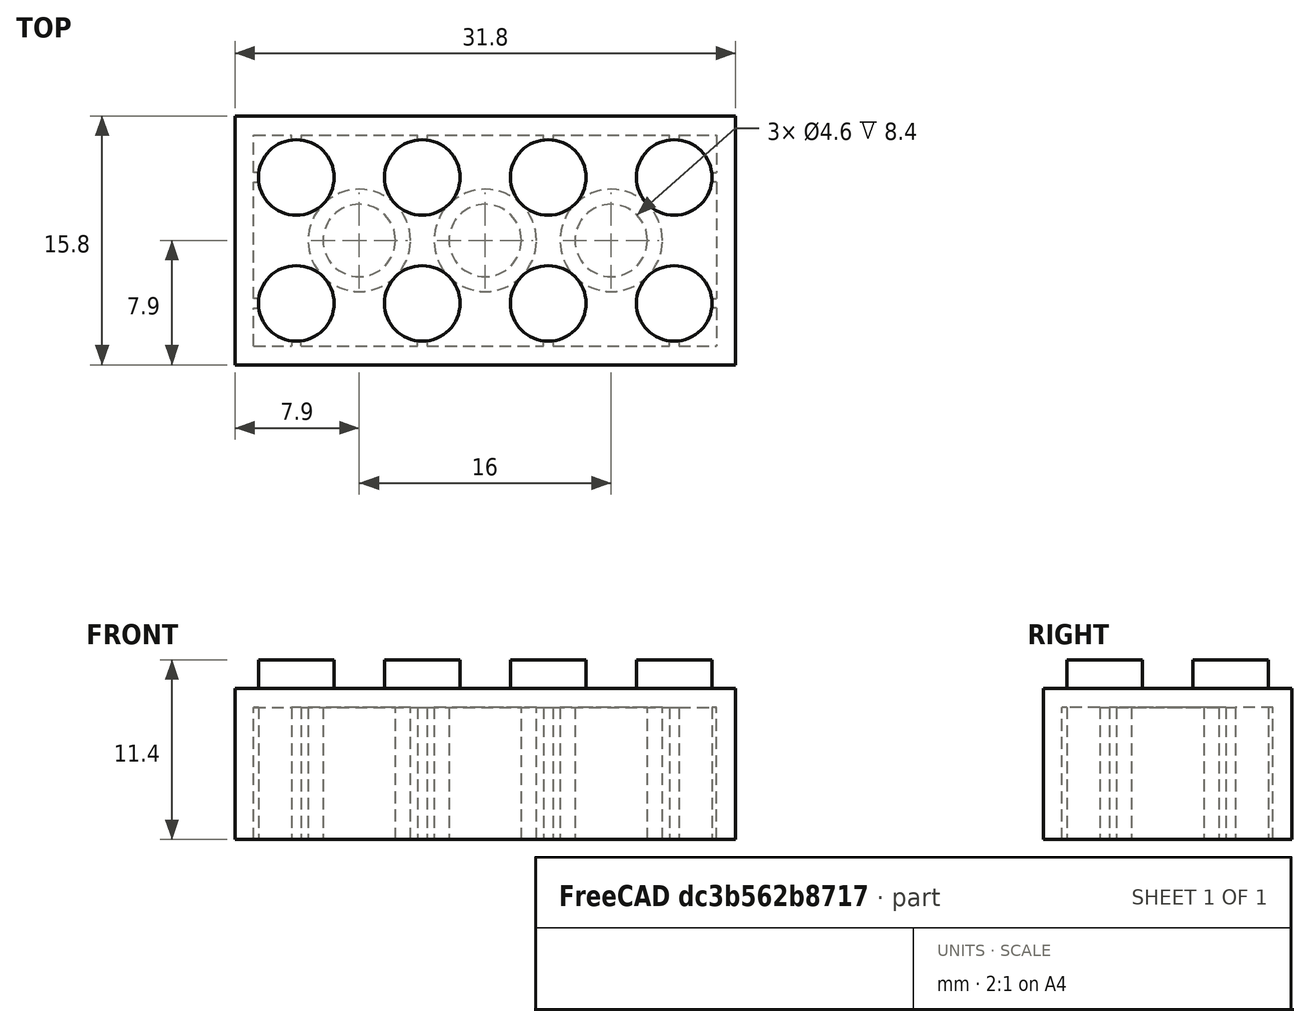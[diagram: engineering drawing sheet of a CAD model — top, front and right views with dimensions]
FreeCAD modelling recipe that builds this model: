
FCSTD DOCUMENT  (FreeCAD 0.20R29410 (Git))
Label: lego_brick
License: All rights reserved
LicenseURL: http://en.wikipedia.org/wiki/All_rights_reserved
objects: TechDraw::DrawViewDimension×13, Sketcher::SketchObject×4, TechDraw::DrawProjGroupItem×4, PartDesign::Pad×3, PartDesign::Pocket×1, PartDesign::Body×1, TechDraw::DrawSVGTemplate×1, TechDraw::DrawViewPart×1, TechDraw::DrawProjGroup×1, TechDraw::DrawViewAnnotation×1, TechDraw::DrawPage×1
note: 13 computed .brp shape members not serialized (recipe doc carries the construction recipe); baked Part::Feature solids carry a one-line shape summary decoded from their .brp

FEATURE [Sketcher::SketchObject] Sketch
  FullyConstrained = true
  MapMode = 5
  Support = -> [XY_Plane]
  sketch-geometry (5):
    g0: LineSegment StartX=-15.9 StartY=7.9 StartZ=0 EndX=-15.9 EndY=-7.9 EndZ=0
    g1: LineSegment StartX=-15.9 StartY=-7.9 StartZ=0 EndX=15.9 EndY=-7.9 EndZ=0
    g2: LineSegment StartX=15.9 StartY=-7.9 StartZ=0 EndX=15.9 EndY=7.9 EndZ=0
    g3: LineSegment StartX=15.9 StartY=7.9 StartZ=0 EndX=-15.9 EndY=7.9 EndZ=0
    g4: GeomPoint X=0 Y=0 Z=0
  constraints (12):
    c: Coincident(g0,g1)
    c: Coincident(g1,g2)
    c: Coincident(g2,g3)
    c: Coincident(g3,g0)
    c: Horizontal(g1)
    c: Horizontal(g3)
    c: Vertical(g0)
    c: Vertical(g2)
    c: Symmetric(g1,g0,g4)
    c: Coincident(g4,g-1)
    c: DistanceY(g2,g2) = 15.8
    c: DistanceX(g3,g3) = 31.8
FEATURE [PartDesign::Pad] Pad
  Direction = (0,0,1)
  Length = 9.6
  Length2 = 10
  Profile = -> Sketch
  ReferenceAxis = -> Sketch [N_Axis]
  Type = 0
FEATURE [Sketcher::SketchObject] Sketch001
  ExternalGeometry = -> [Pad]
  FullyConstrained = true
  MapMode = 5
  Placement = pos=(0,0,9.6) rot=(0,0,1;0rad)
  Support = -> [Pad]
  sketch-geometry (8):
    g0: Circle CenterX=-12 CenterY=4 CenterZ=0 NormalX=0 NormalY=0 NormalZ=1 AngleXU=0 Radius=2.4
    g1: Circle CenterX=-4 CenterY=4 CenterZ=0 NormalX=0 NormalY=0 NormalZ=1 AngleXU=0 Radius=2.4
    g2: Circle CenterX=4 CenterY=4 CenterZ=0 NormalX=0 NormalY=0 NormalZ=1 AngleXU=0 Radius=2.4
    g3: Circle CenterX=12 CenterY=4 CenterZ=0 NormalX=0 NormalY=0 NormalZ=1 AngleXU=0 Radius=2.4
    g4: Circle CenterX=12 CenterY=-4 CenterZ=0 NormalX=0 NormalY=0 NormalZ=1 AngleXU=0 Radius=2.4
    g5: Circle CenterX=4 CenterY=-4 CenterZ=0 NormalX=0 NormalY=0 NormalZ=1 AngleXU=0 Radius=2.4
    g6: Circle CenterX=-4 CenterY=-4 CenterZ=0 NormalX=0 NormalY=0 NormalZ=1 AngleXU=0 Radius=2.4
    g7: Circle CenterX=-12 CenterY=-4 CenterZ=0 NormalX=0 NormalY=0 NormalZ=1 AngleXU=0 Radius=2.4
  constraints (20):
    c: Diameter(g0) = 4.8
    c: Equal(g0,g1)
    c: Equal(g1,g2)
    c: Equal(g2,g3)
    c: Equal(g3,g4)
    c: Equal(g4,g5)
    c: Equal(g5,g6)
    c: Equal(g6,g7)
    c: Symmetric(g0,g7,g-1)
    c: Symmetric(g1,g6,g-1)
    c: Symmetric(g2,g5,g-1)
    c: Symmetric(g3,g4,g-1)
    c: DistanceX(g-3,g0) = 3.9
    c: DistanceY(g0,g-3) = 3.9
    c: DistanceX(g0,g1) = 8
    c: DistanceX(g1,g2) = 8
    c: DistanceX(g2,g3) = 8
    c: Horizontal(g1,g0)
    c: Horizontal(g2,g1)
    c: Horizontal(g3,g2)
FEATURE [PartDesign::Pad] Pad001
  BaseFeature = -> Pad
  Direction = (0,0,1)
  Length = 1.8
  Length2 = 10
  Profile = -> Sketch001
  ReferenceAxis = -> Sketch001 [N_Axis]
  Type = 0
FEATURE [Sketcher::SketchObject] Sketch002
  ExternalGeometry = -> [Pad001]
  FullyConstrained = true
  MapMode = 5
  Placement = pos=(0,0,0) rot=(1,0,0;3.14159rad)
  Support = -> [Pad001]
  sketch-geometry (11):
    g0: LineSegment StartX=-14.7 StartY=6.7 StartZ=0 EndX=-14.7 EndY=-6.7 EndZ=0
    g1: LineSegment StartX=-14.7 StartY=-6.7 StartZ=0 EndX=14.7 EndY=-6.7 EndZ=0
    g2: LineSegment StartX=14.7 StartY=-6.7 StartZ=0 EndX=14.7 EndY=6.7 EndZ=0
    g3: GeomPoint X=0 Y=0 Z=0
    g4: Circle CenterX=0 CenterY=0 CenterZ=0 NormalX=0 NormalY=0 NormalZ=1 AngleXU=0 Radius=2.3
    g5: Circle CenterX=0 CenterY=0 CenterZ=0 NormalX=0 NormalY=0 NormalZ=1 AngleXU=0 Radius=3.25
    g6: Circle CenterX=8 CenterY=0 CenterZ=0 NormalX=0 NormalY=0 NormalZ=1 AngleXU=0 Radius=2.3
    g7: Circle CenterX=8 CenterY=0 CenterZ=0 NormalX=0 NormalY=0 NormalZ=1 AngleXU=0 Radius=3.25
    g8: Circle CenterX=-8 CenterY=0 CenterZ=0 NormalX=0 NormalY=0 NormalZ=1 AngleXU=0 Radius=2.3
    g9: Circle CenterX=-8 CenterY=0 CenterZ=0 NormalX=0 NormalY=0 NormalZ=1 AngleXU=0 Radius=3.25
    g10: LineSegment StartX=-14.7 StartY=6.7 StartZ=0 EndX=14.7 EndY=6.7 EndZ=0
  constraints (26):
    c: Coincident(g0,g1)
    c: Coincident(g1,g2)
    c: Horizontal(g1)
    c: Vertical(g0)
    c: Vertical(g2)
    c: Symmetric(g1,g0,g3)
    c: Coincident(g3,g-1)
    c: DistanceX(g-3,g0) = 1.2
    c: DistanceY(g0,g-3) = 1.2
    c: Coincident(g4,g3)
    c: Diameter(g4) = 4.6
    c: Coincident(g5,g4)
    c: Diameter(g5) = 6.5
    c: PointOnObject(g6,g-1)
    c: Coincident(g7,g6)
    c: PointOnObject(g8,g-1)
    c: Coincident(g9,g8)
    c: Equal(g8,g6)
    c: Equal(g6,g4)
    c: Equal(g9,g5)
    c: Equal(g5,g7)
    c: DistanceX(g4,g6) = 8
    c: DistanceX(g8,g4) = 8
    c: Coincident(g10,g0)
    c: Coincident(g10,g2)
    c: Horizontal(g10)
FEATURE [PartDesign::Pocket] Pocket
  BaseFeature = -> Pad001
  Direction = (0,0,1)
  Length = 8.4
  Length2 = 5
  Profile = -> Sketch002
  ReferenceAxis = -> Sketch002 [N_Axis]
  Type = 0
FEATURE [Sketcher::SketchObject] Sketch003
  ExternalGeometry = -> [Pocket]
  FullyConstrained = true
  MapMode = 5
  Placement = pos=(0,0,8.4) rot=(1,0,0;3.14159rad)
  Support = -> [Pocket]
  sketch-geometry (48):
    g0: LineSegment StartX=-12.3 StartY=6.7 StartZ=0 EndX=-11.7 EndY=6.7 EndZ=0
    g1: LineSegment StartX=-11.7 StartY=6.7 StartZ=0 EndX=-11.7 EndY=6.4 EndZ=0
    g2: LineSegment StartX=-11.7 StartY=6.4 StartZ=0 EndX=-12.3 EndY=6.4 EndZ=0
    g3: LineSegment StartX=-12.3 StartY=6.4 StartZ=0 EndX=-12.3 EndY=6.7 EndZ=0
    g4: LineSegment StartX=4.3 StartY=6.7 StartZ=0 EndX=3.7 EndY=6.7 EndZ=0
    g5: LineSegment StartX=3.7 StartY=6.7 StartZ=0 EndX=3.7 EndY=6.4 EndZ=0
    g6: LineSegment StartX=3.7 StartY=6.4 StartZ=0 EndX=4.3 EndY=6.4 EndZ=0
    g7: LineSegment StartX=4.3 StartY=6.4 StartZ=0 EndX=4.3 EndY=6.7 EndZ=0
    g8: LineSegment StartX=-3.7 StartY=6.7 StartZ=0 EndX=-4.3 EndY=6.7 EndZ=0
    g9: LineSegment StartX=-4.3 StartY=6.7 StartZ=0 EndX=-4.3 EndY=6.4 EndZ=0
    g10: LineSegment StartX=-4.3 StartY=6.4 StartZ=0 EndX=-3.7 EndY=6.4 EndZ=0
    g11: LineSegment StartX=-3.7 StartY=6.4 StartZ=0 EndX=-3.7 EndY=6.7 EndZ=0
    g12: LineSegment StartX=12.3 StartY=6.7 StartZ=0 EndX=11.7 EndY=6.7 EndZ=0
    g13: LineSegment StartX=11.7 StartY=6.7 StartZ=0 EndX=11.7 EndY=6.4 EndZ=0
    g14: LineSegment StartX=11.7 StartY=6.4 StartZ=0 EndX=12.3 EndY=6.4 EndZ=0
    g15: LineSegment StartX=12.3 StartY=6.4 StartZ=0 EndX=12.3 EndY=6.7 EndZ=0
    g16: LineSegment StartX=-14.7 StartY=4.3 StartZ=0 EndX=-14.4 EndY=4.3 EndZ=0
    g17: LineSegment StartX=-14.4 StartY=4.3 StartZ=0 EndX=-14.4 EndY=3.7 EndZ=0
    g18: LineSegment StartX=-14.4 StartY=3.7 StartZ=0 EndX=-14.7 EndY=3.7 EndZ=0
    g19: LineSegment StartX=-14.7 StartY=3.7 StartZ=0 EndX=-14.7 EndY=4.3 EndZ=0
    g20: LineSegment StartX=-14.7 StartY=-3.7 StartZ=0 EndX=-14.4 EndY=-3.7 EndZ=0
    g21: LineSegment StartX=-14.4 StartY=-3.7 StartZ=0 EndX=-14.4 EndY=-4.3 EndZ=0
    g22: LineSegment StartX=-14.4 StartY=-4.3 StartZ=0 EndX=-14.7 EndY=-4.3 EndZ=0
    g23: LineSegment StartX=-14.7 StartY=-4.3 StartZ=0 EndX=-14.7 EndY=-3.7 EndZ=0
    g24: LineSegment StartX=-12.3 StartY=-6.7 StartZ=0 EndX=-11.7 EndY=-6.7 EndZ=0
    g25: LineSegment StartX=-11.7 StartY=-6.7 StartZ=0 EndX=-11.7 EndY=-6.4 EndZ=0
    g26: LineSegment StartX=-11.7 StartY=-6.4 StartZ=0 EndX=-12.3 EndY=-6.4 EndZ=0
    g27: LineSegment StartX=-12.3 StartY=-6.4 StartZ=0 EndX=-12.3 EndY=-6.7 EndZ=0
    g28: LineSegment StartX=-4.3 StartY=-6.7 StartZ=0 EndX=-3.7 EndY=-6.7 EndZ=0
    g29: LineSegment StartX=-3.7 StartY=-6.7 StartZ=0 EndX=-3.7 EndY=-6.4 EndZ=0
    g30: LineSegment StartX=-3.7 StartY=-6.4 StartZ=0 EndX=-4.3 EndY=-6.4 EndZ=0
    g31: LineSegment StartX=-4.3 StartY=-6.4 StartZ=0 EndX=-4.3 EndY=-6.7 EndZ=0
    g32: LineSegment StartX=3.7 StartY=-6.7 StartZ=0 EndX=4.3 EndY=-6.7 EndZ=0
    g33: LineSegment StartX=4.3 StartY=-6.7 StartZ=0 EndX=4.3 EndY=-6.4 EndZ=0
    g34: LineSegment StartX=4.3 StartY=-6.4 StartZ=0 EndX=3.7 EndY=-6.4 EndZ=0
    g35: LineSegment StartX=3.7 StartY=-6.4 StartZ=0 EndX=3.7 EndY=-6.7 EndZ=0
    g36: LineSegment StartX=11.7 StartY=-6.7 StartZ=0 EndX=12.3 EndY=-6.7 EndZ=0
    g37: LineSegment StartX=12.3 StartY=-6.7 StartZ=0 EndX=12.3 EndY=-6.4 EndZ=0
    g38: LineSegment StartX=12.3 StartY=-6.4 StartZ=0 EndX=11.7 EndY=-6.4 EndZ=0
    g39: LineSegment StartX=11.7 StartY=-6.4 StartZ=0 EndX=11.7 EndY=-6.7 EndZ=0
    g40: LineSegment StartX=14.7 StartY=4.3 StartZ=0 EndX=14.4 EndY=4.3 EndZ=0
    g41: LineSegment StartX=14.4 StartY=4.3 StartZ=0 EndX=14.4 EndY=3.7 EndZ=0
    g42: LineSegment StartX=14.4 StartY=3.7 StartZ=0 EndX=14.7 EndY=3.7 EndZ=0
    g43: LineSegment StartX=14.7 StartY=3.7 StartZ=0 EndX=14.7 EndY=4.3 EndZ=0
    g44: LineSegment StartX=14.7 StartY=-3.7 StartZ=0 EndX=14.4 EndY=-3.7 EndZ=0
    g45: LineSegment StartX=14.4 StartY=-3.7 StartZ=0 EndX=14.4 EndY=-4.3 EndZ=0
    g46: LineSegment StartX=14.4 StartY=-4.3 StartZ=0 EndX=14.7 EndY=-4.3 EndZ=0
    g47: LineSegment StartX=14.7 StartY=-4.3 StartZ=0 EndX=14.7 EndY=-3.7 EndZ=0
  constraints (137):
    c: Coincident(g0,g1)
    c: Coincident(g1,g2)
    c: Coincident(g2,g3)
    c: Coincident(g3,g0)
    c: Horizontal(g0)
    c: Horizontal(g2)
    c: Vertical(g1)
    c: Vertical(g3)
    c: DistanceX(g-3,g0) = 3.6
    c: Coincident(g4,g5)
    c: Coincident(g5,g6)
    c: Coincident(g6,g7)
    c: Coincident(g7,g4)
    c: Horizontal(g4)
    c: Horizontal(g6)
    c: Vertical(g5)
    c: Vertical(g7)
    c: PointOnObject(g4,g-8)
    c: Coincident(g8,g9)
    c: Coincident(g9,g10)
    c: Coincident(g10,g11)
    c: Coincident(g11,g8)
    c: Horizontal(g8)
    c: Horizontal(g10)
    c: Vertical(g9)
    c: Vertical(g11)
    c: Coincident(g12,g13)
    c: Coincident(g13,g14)
    c: Coincident(g14,g15)
    c: Coincident(g15,g12)
    c: Horizontal(g12)
    c: Horizontal(g14)
    c: Vertical(g13)
    c: Vertical(g15)
    c: PointOnObject(g12,g-8)
    c: DistanceY(g2,g0) = 0.3
    c: DistanceX(g0,g0) = 0.6
    c: Equal(g2,g6)
    c: Equal(g6,g10)
    c: Equal(g10,g14)
    c: Equal(g1,g5)
    c: Equal(g9,g13)
    c: Symmetric(g4,g8,g-2)
    c: DistanceX(g-3,g8) = 11.6
    c: Coincident(g16,g17)
    c: Coincident(g17,g18)
    c: Coincident(g18,g19)
    c: Coincident(g19,g16)
    c: Horizontal(g16)
    c: Horizontal(g18)
    c: Vertical(g17)
    c: Vertical(g19)
    c: PointOnObject(g16,g-4)
    c: Coincident(g20,g21)
    c: Coincident(g21,g22)
    c: Coincident(g22,g23)
    c: Coincident(g23,g20)
    c: Horizontal(g20)
    c: Horizontal(g22)
    c: Vertical(g21)
    c: Vertical(g23)
    c: PointOnObject(g20,g-4)
    c: DistanceY(g18,g16) = 0.6
    c: DistanceX(g16,g16) = 0.3
    c: Equal(g18,g20)
    c: Equal(g21,g17)
    c: DistanceY(g16,g-3) = 3.6
    c: DistanceY(g-9,g22) = 3.6
    c: Coincident(g24,g25)
    c: Coincident(g25,g26)
    c: Coincident(g26,g27)
    c: Coincident(g27,g24)
    c: Horizontal(g24)
    c: Horizontal(g26)
    c: Vertical(g25)
    c: Vertical(g27)
    c: PointOnObject(g24,g-5)
    c: Coincident(g28,g29)
    c: Coincident(g29,g30)
    c: Coincident(g30,g31)
    c: Coincident(g31,g28)
    c: Horizontal(g28)
    c: Horizontal(g30)
    c: Vertical(g29)
    c: Vertical(g31)
    c: PointOnObject(g28,g-5)
    c: Coincident(g32,g33)
    c: Coincident(g33,g34)
    c: Coincident(g34,g35)
    c: Coincident(g35,g32)
    c: Horizontal(g32)
    c: Horizontal(g34)
    c: Vertical(g33)
    c: Vertical(g35)
    c: Coincident(g36,g37)
    c: Coincident(g37,g38)
    c: Coincident(g38,g39)
    c: Coincident(g39,g36)
    c: Horizontal(g36)
    c: Horizontal(g38)
    c: Vertical(g37)
    c: Vertical(g39)
    c: PointOnObject(g36,g-5)
    c: Equal(g38,g14)
    c: Equal(g14,g34)
    c: Equal(g34,g30)
    c: Equal(g30,g26)
    c: Equal(g37,g7)
    c: Equal(g7,g33)
    c: Symmetric(g2,g26,g-1)
    c: Symmetric(g30,g9,g-1)
    c: Symmetric(g34,g5,g-1)
    c: Symmetric(g38,g13,g-1)
    c: Coincident(g40,g41)
    c: Coincident(g41,g42)
    c: Coincident(g42,g43)
    c: Coincident(g43,g40)
    c: Horizontal(g40)
    c: Horizontal(g42)
    c: Vertical(g41)
    c: Vertical(g43)
    c: PointOnObject(g40,g-6)
    c: Coincident(g44,g45)
    c: Coincident(g45,g46)
    c: Coincident(g46,g47)
    c: Coincident(g47,g44)
    c: Horizontal(g44)
    c: Horizontal(g46)
    c: Vertical(g45)
    c: Vertical(g47)
    c: PointOnObject(g44,g-6)
    c: Equal(g17,g41)
    c: Equal(g41,g45)
    c: Symmetric(g40,g16,g-2)
    c: Symmetric(g45,g21,g-2)
    c: DistanceX(g12,g-7) = 3.6
    c: PointOnObject(g0,g-8)
FEATURE [PartDesign::Pad] Pad002
  BaseFeature = -> Pocket
  Direction = (0,0,-1)
  Length = 8.4
  Length2 = 10
  Profile = -> Sketch003
  ReferenceAxis = -> Sketch003 [N_Axis]
  Type = 0
FEATURE [PartDesign::Body] Body  label="LegoBrick2x4"
  Group = -> [Sketch,Pad,Sketch001,Pad001,Sketch002,Pocket,Sketch003,Pad002]
  Origin = -> Origin
  Tip = -> Pad002
FEATURE [TechDraw::DrawSVGTemplate] Template
  Height = 297
  Orientation = 0
  Width = 210
FEATURE [TechDraw::DrawViewPart] View
  Caption = 3D View
  CoarseView = false
  Direction = (0.378,-0.742,0.554)
  Focus = 100
  HardHidden = false
  IsoCount = 0
  IsoHidden = false
  IsoVisible = false
  LockPosition = false
  Perspective = false
  Rotation = 0
  Scale = 2
  ScaleType = 2
  SeamHidden = false
  SeamVisible = true
  SmoothHidden = false
  SmoothVisible = true
  Source = -> [Body]
  X = 58.5961
  XDirection = (0.887,0.462,0.013)
  Y = 233.477
FEATURE [TechDraw::DrawProjGroupItem] ProjItem  label="Front"
  Caption = Front View
  CoarseView = false
  Direction = (0,-1,0)
  Focus = 100
  HardHidden = false
  IsoCount = 0
  IsoHidden = false
  IsoVisible = false
  LockPosition = true
  Perspective = false
  Rotation = 0
  RotationVector = (1,0,0)
  ScaleType = 2
  SeamHidden = false
  SeamVisible = true
  SmoothHidden = false
  SmoothVisible = true
  Source = -> [Body]
  Type = 0
  X = 0
  XDirection = (1,0,2e-16)
  Y = 0
FEATURE [TechDraw::DrawProjGroupItem] ProjItem001  label="Right"
  Caption = Left View
  CoarseView = false
  Direction = (1,-1e-16,2e-16)
  Focus = 100
  HardHidden = false
  IsoCount = 0
  IsoHidden = false
  IsoVisible = false
  LockPosition = false
  Perspective = false
  Rotation = 0
  RotationVector = (1,0,0)
  ScaleType = 2
  SeamHidden = false
  SeamVisible = true
  SmoothHidden = false
  SmoothVisible = true
  Source = -> [Body]
  Type = 2
  X = -52.0285
  XDirection = (1e-16,1,0)
  Y = 0
FEATURE [TechDraw::DrawProjGroupItem] ProjItem003  label="Top"
  Caption = Top View
  CoarseView = false
  Direction = (-2e-16,0,1)
  Focus = 100
  HardHidden = false
  IsoCount = 0
  IsoHidden = false
  IsoVisible = false
  LockPosition = false
  Perspective = false
  Rotation = 0
  RotationVector = (1,0,0)
  ScaleType = 2
  SeamHidden = false
  SeamVisible = true
  SmoothHidden = false
  SmoothVisible = true
  Source = -> [Body]
  Type = 4
  X = 0
  XDirection = (1,0,2e-16)
  Y = 38.3342
FEATURE [TechDraw::DrawProjGroupItem] ProjItem004  label="Bottom"
  Caption = Bottom View
  CoarseView = false
  Direction = (2e-16,0,-1)
  Focus = 100
  HardHidden = false
  IsoCount = 0
  IsoHidden = false
  IsoVisible = false
  LockPosition = false
  Perspective = false
  Rotation = 0
  RotationVector = (1,0,0)
  ScaleType = 2
  SeamHidden = false
  SeamVisible = true
  SmoothHidden = false
  SmoothVisible = true
  Source = -> [Body]
  Type = 5
  X = 0
  XDirection = (1,0,2e-16)
  Y = -57.8041
FEATURE [TechDraw::DrawProjGroup] ProjGroup
  Anchor = -> ProjItem
  AutoDistribute = false
  LockPosition = false
  ProjectionType = 0
  Rotation = 0
  ScaleType = 2
  Source = -> [Body]
  Views = -> [ProjItem,ProjItem001,ProjItem003,ProjItem004]
  X = 110.766
  Y = 108.956
  spacingX = 10
  spacingY = 15
FEATURE [TechDraw::DrawViewDimension] Dimension003
  AngleOverride = false
  Arbitrary = false
  ArbitraryTolerances = false
  EqualTolerance = true
  ExtensionAngle = 0
  FormatSpec = %.2w
  FormatSpecOverTolerance = %+.2w
  FormatSpecUnderTolerance = %+.2w
  Inverted = false
  LineAngle = 0
  LockPosition = false
  MeasureType = 1
  OverTolerance = 0
  References2D = -> [ProjItem003]
  Rotation = 0
  ScaleType = 0
  TheoreticalExact = false
  Type = 1
  UnderTolerance = 0
  X = -24.2592
  Y = 27.8106
FEATURE [TechDraw::DrawViewDimension] Dimension004
  AngleOverride = false
  Arbitrary = false
  ArbitraryTolerances = false
  EqualTolerance = true
  ExtensionAngle = 0
  FormatSpec = %.2w
  FormatSpecOverTolerance = %+.2w
  FormatSpecUnderTolerance = %+.2w
  Inverted = false
  LineAngle = 0
  LockPosition = false
  MeasureType = 1
  OverTolerance = 0
  References2D = -> [ProjItem003]
  Rotation = 0
  ScaleType = 0
  TheoreticalExact = false
  Type = 1
  UnderTolerance = 0
  X = -0.11096
  Y = 37.5852
FEATURE [TechDraw::DrawViewDimension] Dimension
  AngleOverride = false
  Arbitrary = false
  ArbitraryTolerances = false
  EqualTolerance = true
  ExtensionAngle = 0
  FormatSpec = %.2w
  FormatSpecOverTolerance = %+.2w
  FormatSpecUnderTolerance = %+.2w
  Inverted = false
  LineAngle = 0
  LockPosition = false
  MeasureType = 1
  OverTolerance = 0
  References2D = -> [ProjItem003]
  Rotation = 0
  ScaleType = 0
  TheoreticalExact = false
  Type = 2
  UnderTolerance = 0
  X = -34.7789
  Y = -7.10758
FEATURE [TechDraw::DrawViewDimension] Dimension005
  AngleOverride = false
  Arbitrary = false
  ArbitraryTolerances = false
  EqualTolerance = true
  ExtensionAngle = 0
  FormatSpec = %.2w
  FormatSpecOverTolerance = %+.2w
  FormatSpecUnderTolerance = %+.2w
  Inverted = false
  LineAngle = 0
  LockPosition = false
  MeasureType = 1
  OverTolerance = 0
  References2D = -> [ProjItem003]
  Rotation = 0
  ScaleType = 0
  TheoreticalExact = false
  Type = 2
  UnderTolerance = 0
  X = 27.5932
  Y = 23.9254
FEATURE [TechDraw::DrawViewDimension] Dimension006
  AngleOverride = false
  Arbitrary = false
  ArbitraryTolerances = false
  EqualTolerance = true
  ExtensionAngle = 0
  FormatSpec = ⌀%.2w
  FormatSpecOverTolerance = %+.2w
  FormatSpecUnderTolerance = %+.2w
  Inverted = false
  LineAngle = 0
  LockPosition = false
  MeasureType = 1
  OverTolerance = 0
  References2D = -> [ProjItem003]
  Rotation = 0
  ScaleType = 0
  TheoreticalExact = false
  Type = 5
  UnderTolerance = 0
  X = 46.2217
  Y = 1.27628
FEATURE [TechDraw::DrawViewDimension] Dimension007
  AngleOverride = false
  Arbitrary = false
  ArbitraryTolerances = false
  EqualTolerance = true
  ExtensionAngle = 0
  FormatSpec = %.2w
  FormatSpecOverTolerance = %+.2w
  FormatSpecUnderTolerance = %+.2w
  Inverted = false
  LineAngle = 0
  LockPosition = false
  MeasureType = 1
  OverTolerance = 0
  References2D = -> [ProjItem001]
  Rotation = 0
  ScaleType = 0
  TheoreticalExact = false
  Type = 2
  UnderTolerance = 0
  X = -22.6616
  Y = 20.3718
FEATURE [TechDraw::DrawViewDimension] Dimension008
  AngleOverride = false
  Arbitrary = false
  ArbitraryTolerances = false
  EqualTolerance = true
  ExtensionAngle = 0
  FormatSpec = %.2w
  FormatSpecOverTolerance = %+.2w
  FormatSpecUnderTolerance = %+.2w
  Inverted = false
  LineAngle = 0
  LockPosition = false
  MeasureType = 1
  OverTolerance = 0
  References2D = -> [ProjItem004]
  Rotation = 0
  ScaleType = 0
  TheoreticalExact = false
  Type = 1
  UnderTolerance = 0
  X = -25.403
  Y = 25.2966
FEATURE [TechDraw::DrawViewDimension] Dimension010
  AngleOverride = false
  Arbitrary = false
  ArbitraryTolerances = false
  EqualTolerance = true
  ExtensionAngle = 0
  FormatSpec = %.2w
  FormatSpecOverTolerance = %+.2w
  FormatSpecUnderTolerance = %+.2w
  Inverted = false
  LineAngle = 0
  LockPosition = false
  MeasureType = 1
  OverTolerance = 0
  References2D = -> [ProjItem004]
  Rotation = 0
  ScaleType = 0
  TheoreticalExact = false
  Type = 1
  UnderTolerance = 0
  X = 30.1222
  Y = 21.9388
FEATURE [TechDraw::DrawViewDimension] Dimension011
  AngleOverride = false
  Arbitrary = false
  ArbitraryTolerances = false
  EqualTolerance = true
  ExtensionAngle = 0
  FormatSpec = %.2w
  FormatSpecOverTolerance = %+.2w
  FormatSpecUnderTolerance = %+.2w
  Inverted = false
  LineAngle = 0
  LockPosition = false
  MeasureType = 1
  OverTolerance = 0
  References2D = -> [ProjItem004]
  Rotation = 0
  ScaleType = 0
  TheoreticalExact = false
  Type = 2
  UnderTolerance = 0
  X = -27.6709
  Y = -4.83854
FEATURE [TechDraw::DrawViewDimension] Dimension013
  AngleOverride = false
  Arbitrary = false
  ArbitraryTolerances = false
  EqualTolerance = true
  ExtensionAngle = 0
  FormatSpec = ⌀%.2w
  FormatSpecOverTolerance = %+.2w
  FormatSpecUnderTolerance = %+.2w
  Inverted = false
  LineAngle = 0
  LockPosition = false
  MeasureType = 1
  OverTolerance = 0
  References2D = -> [ProjItem004]
  Rotation = 0
  ScaleType = 0
  TheoreticalExact = false
  Type = 5
  UnderTolerance = 0
  X = 35.0603
  Y = 10.8649
FEATURE [TechDraw::DrawViewDimension] Dimension014
  AngleOverride = false
  Arbitrary = false
  ArbitraryTolerances = false
  EqualTolerance = true
  ExtensionAngle = 0
  FormatSpec = ⌀%.2w
  FormatSpecOverTolerance = %+.2w
  FormatSpecUnderTolerance = %+.2w
  Inverted = false
  LineAngle = 0
  LockPosition = false
  MeasureType = 1
  OverTolerance = 0
  References2D = -> [ProjItem004]
  Rotation = 0
  ScaleType = 0
  TheoreticalExact = false
  Type = 5
  UnderTolerance = 0
  X = 36.2932
  Y = 3.39045
FEATURE [TechDraw::DrawViewDimension] Dimension015
  AngleOverride = false
  Arbitrary = false
  ArbitraryTolerances = false
  EqualTolerance = true
  ExtensionAngle = 0
  FormatSpec = %.2w
  FormatSpecOverTolerance = %+.2w
  FormatSpecUnderTolerance = %+.2w
  Inverted = false
  LineAngle = 0
  LockPosition = false
  MeasureType = 1
  OverTolerance = 0
  References2D = -> [ProjItem004]
  Rotation = 0
  ScaleType = 0
  TheoreticalExact = false
  Type = 1
  UnderTolerance = 0
  X = 30.3806
  Y = 28.948
FEATURE [TechDraw::DrawViewDimension] Dimension012
  AngleOverride = false
  Arbitrary = false
  ArbitraryTolerances = false
  EqualTolerance = true
  ExtensionAngle = 0
  FormatSpec = %.2w
  FormatSpecOverTolerance = %+.2w
  FormatSpecUnderTolerance = %+.2w
  Inverted = false
  LineAngle = 0
  LockPosition = false
  MeasureType = 1
  OverTolerance = 0
  References2D = -> [ProjItem004]
  Rotation = 0
  ScaleType = 0
  TheoreticalExact = false
  Type = 1
  UnderTolerance = 0
  X = 28.0151
  Y = 35.2117
FEATURE [TechDraw::DrawViewAnnotation] Annotation
  Font = osifont
  LineSpace = 80
  LockPosition = false
  MaxWidth = -1
  Rotation = 0
  ScaleType = 0
  Text = Lego Brick
  TextSize = 14
  TextStyle = 0
  X = 154.981
  Y = 231.691
FEATURE [TechDraw::DrawPage] Page
  KeepUpdated = true
  NextBalloonIndex = 1
  ProjectionType = 0
  Template = -> Template
  Views = -> [View,ProjGroup,Dimension003,Dimension004,Dimension,Dimension005,Dimension006,Dimension007,Dimension008,Dimension010,Dimension011,Dimension012,Dimension013,Dimension014,Dimension015,Annotation]
